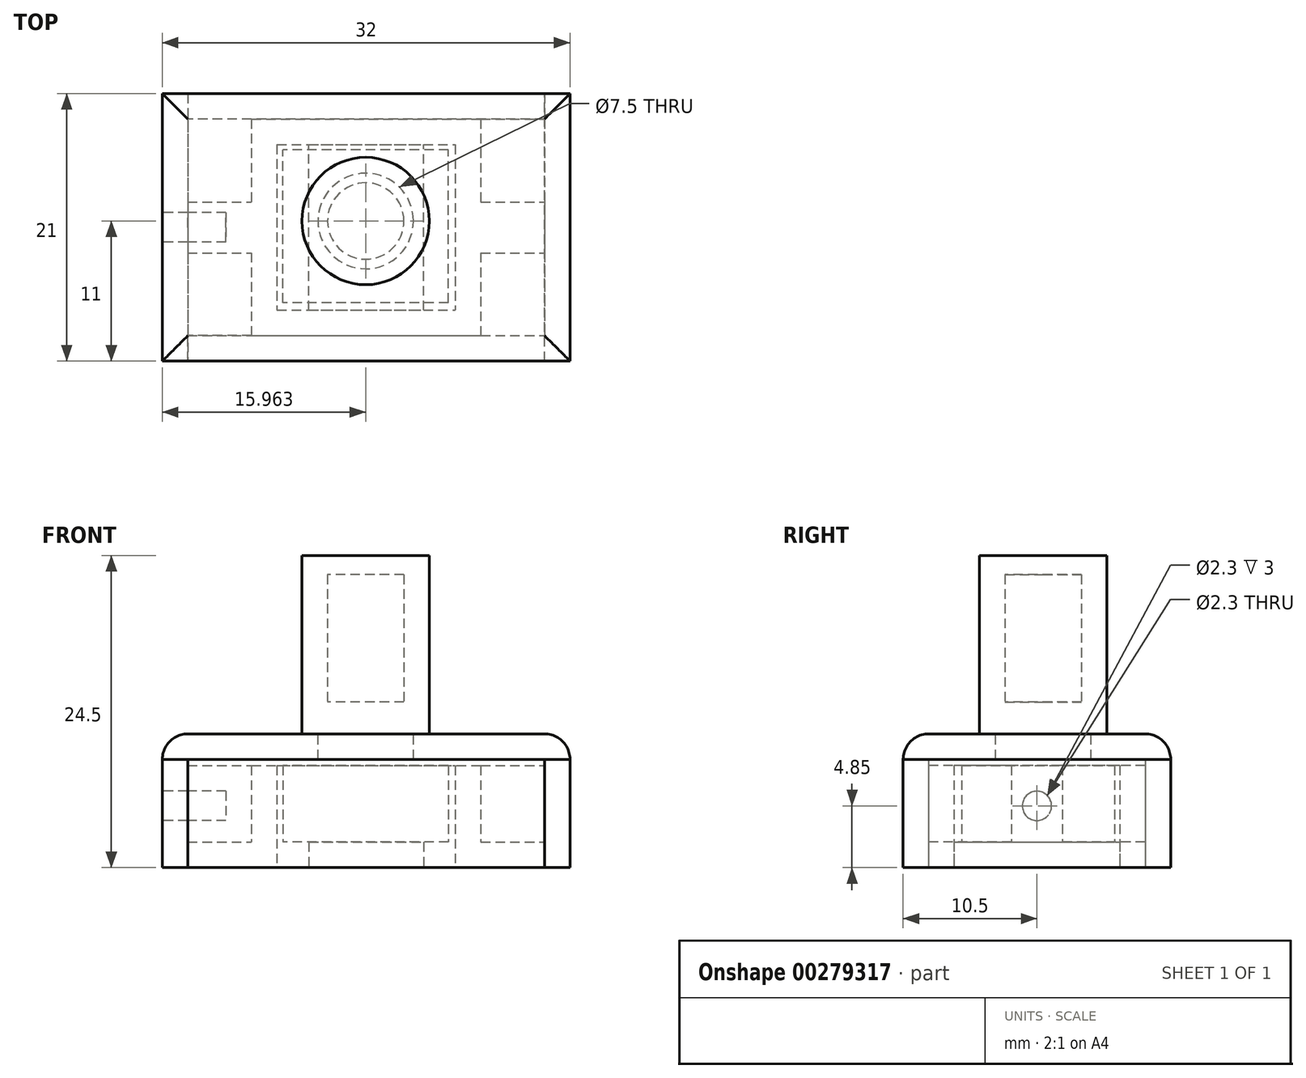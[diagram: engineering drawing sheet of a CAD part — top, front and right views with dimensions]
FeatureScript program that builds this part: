
annotation { "Feature Type Name" : "Feature", "Feature Type Description" : "" }
export const myFeature = defineFeature(function(context is Context, id is Id, definition is map)
    precondition{}
    {
        {
            var Q0;
            Q0=qCreatedBy(makeId("Top.planeOp"),FACE);
            var sketch = newSketch(context, id + "F0", { "sketchPlane" : qUnion([Q0])});
            skLineSegment(sketch, "E0.bottom", {"start": v(-2, 2) * mm, "end": v(16, 2) * mm});
            skLineSegment(sketch, "E0.top", {"start": v(-2, -15) * mm, "end": v(16, -15) * mm});
            skLineSegment(sketch, "E0.left", {"start": v(-2, 2) * mm, "end": v(-2, -15) * mm});
            skLineSegment(sketch, "E0.right", {"start": v(16, 2) * mm, "end": v(16, -15) * mm});
            skLineSegment(sketch, "E1.bottom", {"start": v(0, 0) * mm, "end": v(14, 0) * mm});
            skLineSegment(sketch, "E1.top", {"start": v(0, -13) * mm, "end": v(14, -13) * mm});
            skLineSegment(sketch, "E1.left", {"start": v(0, 0) * mm, "end": v(0, -13) * mm});
            skLineSegment(sketch, "E1.right", {"start": v(14, 0) * mm, "end": v(14, -13) * mm});
            skSolve(sketch);
        }
        {
            var Q0;
            Q0=qSketchRegion(id+"F0",true);
            extrude(context, id + "F1", {"entities" : qUnion([Q0]), "depth" : 8 * mm});
        }
        {
            var Q0;
            Q0=makeQuery(id+"F1.opExtrude","CAP_FACE",FACE,{"disambiguationData":[OSD([sQuery(id+"F0.wireOp",EDGE,"E0.bottom"),sQuery(id+"F0.wireOp",EDGE,"E0.top"),sQuery(id+"F0.wireOp",EDGE,"E0.left"),sQuery(id+"F0.wireOp",EDGE,"E0.right"),sQuery(id+"F0.wireOp",EDGE,"E1.bottom"),sQuery(id+"F0.wireOp",EDGE,"E1.top"),sQuery(id+"F0.wireOp",EDGE,"E1.left"),sQuery(id+"F0.wireOp",EDGE,"E1.right")])],"isStart":true});
            var sketch = newSketch(context, id + "F2", { "sketchPlane" : qUnion([Q0])});
            skLineSegment(sketch, "E2.bottom", {"start": v(2.5, 13) * mm, "end": v(11.5, 13) * mm});
            skLineSegment(sketch, "E2.top", {"start": v(2.5, 0) * mm, "end": v(11.5, 0) * mm});
            skLineSegment(sketch, "E2.left", {"start": v(2.5, 13) * mm, "end": v(2.5, 0) * mm});
            skLineSegment(sketch, "E2.right", {"start": v(11.5, 13) * mm, "end": v(11.5, 0) * mm});
            skSolve(sketch);
        }
        {
            var Q0;
            Q0=qSketchRegion(id+"F2",true);
            extrude(context, id + "F3", {"entities" : qUnion([Q0]), "operationType" : NewBodyOperationType.ADD, "oppositeDirection" : true, "depth" : 2 * mm});
        }
        {
            var Q0;
            Q0=makeQuery(id+"F3.opExtrude","CAP_FACE",FACE,{"disambiguationData":[OSD([sQuery(id+"F2.wireOp",EDGE,"E2.bottom"),sQuery(id+"F2.wireOp",EDGE,"E2.top"),sQuery(id+"F2.wireOp",EDGE,"E2.left"),sQuery(id+"F2.wireOp",EDGE,"E2.right")])],"isStart":false});
            var sketch = newSketch(context, id + "F4", { "sketchPlane" : qUnion([Q0])});
            skSolve(sketch);
        }
        {
            var Q0;
            Q0=makeQuery(id+"F4.imprint","IMPRINT",FACE,{"disambiguationData":[TD([[makeQuery(id+"F4.imprint","IMPRINT",EDGE,{"derivedFrom":makeQuery(id+"F3.opExtrude","CAP_EDGE",EDGE,{"disambiguationData":[OSD([sQuery(id+"F2.wireOp",EDGE,"E2.left")])],"isStart":false})}),-1.0]])]});
            var sketch = newSketch(context, id + "F5", { "sketchPlane" : qUnion([Q0])});
            skLineSegment(sketch, "E3.bottom", {"start": v(13.46, -12.41) * mm, "end": v(0.46, -12.41) * mm});
            skLineSegment(sketch, "E3.top", {"start": v(13.46, -0.41) * mm, "end": v(0.46, -0.41) * mm});
            skLineSegment(sketch, "E3.left", {"start": v(13.46, -12.41) * mm, "end": v(13.46, -0.41) * mm});
            skLineSegment(sketch, "E3.right", {"start": v(0.46, -12.41) * mm, "end": v(0.46, -0.41) * mm});
            skPoint(sketch, "E3.middle", {"position": v(6.96, -6.41) * mm});
            skSolve(sketch);
        }
        {
            var Q0;
            Q0=qSketchRegion(id+"F5",true);
            extrude(context, id + "F6", {"entities" : qUnion([Q0]), "depth" : 6 * mm});
        }
        {
            var Q0;
            Q0=makeQuery(id+"F6.opExtrude","CAP_FACE",FACE,{"disambiguationData":[OSD([sQuery(id+"F5.wireOp",EDGE,"E3.bottom"),sQuery(id+"F5.wireOp",EDGE,"E3.top"),sQuery(id+"F5.wireOp",EDGE,"E3.left"),sQuery(id+"F5.wireOp",EDGE,"E3.right")])],"isStart":false});
            var sketch = newSketch(context, id + "F7", { "sketchPlane" : qUnion([Q0])});
            skCircle(sketch, "E4", {"center": v(6.96, -6) * mm, "radius": 3.5 * mm});
            skSolve(sketch);
        }
        {
            var Q0;
            Q0=qSketchRegion(id+"F7",true);
            extrude(context, id + "F8", {"entities" : qUnion([Q0]), "depth" : 5 * mm});
        }
        {
            var Q0;
            Q0=makeQuery(id+"F8.opExtrude","CAP_FACE",FACE,{"disambiguationData":[OSD([sQuery(id+"F7.wireOp",EDGE,"E4")])],"isStart":false});
            var sketch = newSketch(context, id + "F9", { "sketchPlane" : qUnion([Q0])});
            skCircle(sketch, "E5", {"center": v(6.96, -6) * mm, "radius": 3 * mm});
            skSolve(sketch);
        }
        {
            var Q0;
            Q0=qSketchRegion(id+"F9",true);
            extrude(context, id + "F10", {"entities" : qUnion([Q0]), "depth" : 10 * mm});
        }
        {
            var Q0;
            Q0=qCreatedBy(makeId("Top.planeOp"),FACE);
            var sketch = newSketch(context, id + "F11", { "sketchPlane" : qUnion([Q0])});
            skLineSegment(sketch, "E6.bottom", {"start": v(-2, 2) * mm, "end": v(-7, 2) * mm});
            skLineSegment(sketch, "E6.top", {"start": v(-2, -15) * mm, "end": v(-7, -15) * mm});
            skLineSegment(sketch, "E6.left", {"start": v(-2, 2) * mm, "end": v(-2, -15) * mm});
            skLineSegment(sketch, "E6.right", {"start": v(-7, 2) * mm, "end": v(-7, -15) * mm});
            skLineSegment(sketch, "E7.bottom", {"start": v(16, 2) * mm, "end": v(21, 2) * mm});
            skLineSegment(sketch, "E7.top", {"start": v(16, -15) * mm, "end": v(21, -15) * mm});
            skLineSegment(sketch, "E7.left", {"start": v(16, 2) * mm, "end": v(16, -15) * mm});
            skLineSegment(sketch, "E7.right", {"start": v(21, 2) * mm, "end": v(21, -15) * mm});
            skSolve(sketch);
        }
        {
            var Q0;
            Q0=qSketchRegion(id+"F11",true);
            extrude(context, id + "F12", {"entities" : qUnion([Q0]), "operationType" : NewBodyOperationType.ADD, "depth" : 2 * mm});
        }
        {
            var Q0;
            Q0=makeQuery(id+"F12.opExtrude","CAP_FACE",FACE,{"disambiguationData":[OSD([sQuery(id+"F11.wireOp",EDGE,"E6.bottom"),sQuery(id+"F11.wireOp",EDGE,"E6.top"),sQuery(id+"F11.wireOp",EDGE,"E6.left"),sQuery(id+"F11.wireOp",EDGE,"E6.right"),sQuery(id+"F11.wireOp",EDGE,"gcyy9ogg-o8VV-Q8VI-mciE-UxV4sGVMyMyK"),sQuery(id+"F11.wireOp",EDGE,"7D3NRwDX-bBHB-H0ax-FCWy-7Xh7mBDSAGuq")])],"isStart":false});
            var sketch = newSketch(context, id + "F13", { "sketchPlane" : qUnion([Q0])});
            skLineSegment(sketch, "E8.bottom", {"start": v(-7, -4.5) * mm, "end": v(-2, -4.5) * mm});
            skLineSegment(sketch, "E8.top", {"start": v(-7, -8.5) * mm, "end": v(-2, -8.5) * mm});
            skLineSegment(sketch, "E8.left", {"start": v(-7, -4.5) * mm, "end": v(-7, -8.5) * mm});
            skLineSegment(sketch, "E8.right", {"start": v(-2, -4.5) * mm, "end": v(-2, -8.5) * mm});
            skLineSegment(sketch, "E9.bottom", {"start": v(16, -4.5) * mm, "end": v(21, -4.5) * mm});
            skLineSegment(sketch, "E9.top", {"start": v(16, -8.5) * mm, "end": v(21, -8.5) * mm});
            skLineSegment(sketch, "E9.left", {"start": v(16, -4.5) * mm, "end": v(16, -8.5) * mm});
            skLineSegment(sketch, "E9.right", {"start": v(21, -4.5) * mm, "end": v(21, -8.5) * mm});
            skSolve(sketch);
        }
        {
            var Q0;
            Q0=qSketchRegion(id+"F13",true);
            extrude(context, id + "F14", {"entities" : qUnion([Q0]), "operationType" : NewBodyOperationType.ADD, "depth" : 6 * mm});
        }
        {
            var Q0;
            Q0=makeQuery(id+"F12.boolean.opBoolean","MERGE",FACE,{"derivedFrom":[makeQuery(id+"F1.opExtrude","SWEPT_FACE",FACE,{"disambiguationData":[OSD([sQuery(id+"F0.wireOp",EDGE,"E0.top")])]}),makeQuery(id+"F12.opExtrude","SWEPT_FACE",FACE,{"disambiguationData":[OSD([sQuery(id+"F11.wireOp",EDGE,"E6.top")])]}),makeQuery(id+"F12.opExtrude","SWEPT_FACE",FACE,{"disambiguationData":[OSD([sQuery(id+"F11.wireOp",EDGE,"E7.top")])]})]});
            var sketch = newSketch(context, id + "F15", { "sketchPlane" : qUnion([Q0])});
            skLineSegment(sketch, "E10.bottom", {"start": v(-7, 0) * mm, "end": v(21, 0) * mm});
            skLineSegment(sketch, "E10.top", {"start": v(-7, 8.5) * mm, "end": v(21, 8.5) * mm});
            skLineSegment(sketch, "E10.left", {"start": v(-7, 0) * mm, "end": v(-7, 8.5) * mm});
            skLineSegment(sketch, "E10.right", {"start": v(21, 0) * mm, "end": v(21, 8.5) * mm});
            skSolve(sketch);
        }
        {
            var Q0;
            Q0=qSketchRegion(id+"F15",true);
            extrude(context, id + "F16", {"entities" : qUnion([Q0]), "depth" : 2 * mm});
        }
        {
            var Q0;
            Q0=makeQuery(id+"F14.opExtrude","SWEPT_FACE",FACE,{"disambiguationData":[OSD([sQuery(id+"F13.wireOp",EDGE,"E9.right")])]});
            var sketch = newSketch(context, id + "F17", { "sketchPlane" : qUnion([Q0])});
            skLineSegment(sketch, "E11.bottom", {"start": v(-17, 0) * mm, "end": v(4, 0) * mm});
            skLineSegment(sketch, "E11.top", {"start": v(-17, 8.5) * mm, "end": v(4, 8.5) * mm});
            skLineSegment(sketch, "E11.left", {"start": v(-17, 0) * mm, "end": v(-17, 8.5) * mm});
            skLineSegment(sketch, "E11.right", {"start": v(4, 0) * mm, "end": v(4, 8.5) * mm});
            skSolve(sketch);
        }
        {
            var Q0;
            Q0=qSketchRegion(id+"F17",true);
            extrude(context, id + "F18", {"entities" : qUnion([Q0]), "depth" : 2 * mm});
        }
        {
            var Q0;
            Q0=makeQuery(id+"F12.boolean.opBoolean","MERGE",FACE,{"derivedFrom":[makeQuery(id+"F1.opExtrude","SWEPT_FACE",FACE,{"disambiguationData":[OSD([sQuery(id+"F0.wireOp",EDGE,"E0.bottom")])]}),makeQuery(id+"F12.opExtrude","SWEPT_FACE",FACE,{"disambiguationData":[OSD([sQuery(id+"F11.wireOp",EDGE,"E6.bottom")])]}),makeQuery(id+"F12.opExtrude","SWEPT_FACE",FACE,{"disambiguationData":[OSD([sQuery(id+"F11.wireOp",EDGE,"E7.bottom")])]})]});
            var sketch = newSketch(context, id + "F19", { "sketchPlane" : qUnion([Q0])});
            skLineSegment(sketch, "E12.bottom", {"start": v(-21, 0) * mm, "end": v(7, 0) * mm});
            skLineSegment(sketch, "E12.top", {"start": v(-21, 8.5) * mm, "end": v(7, 8.5) * mm});
            skLineSegment(sketch, "E12.left", {"start": v(-21, 0) * mm, "end": v(-21, 8.5) * mm});
            skLineSegment(sketch, "E12.right", {"start": v(7, 0) * mm, "end": v(7, 8.5) * mm});
            skSolve(sketch);
        }
        {
            var Q0;
            Q0=qSketchRegion(id+"F19",true);
            extrude(context, id + "F20", {"entities" : qUnion([Q0]), "depth" : 2 * mm});
        }
        {
            var Q0;
            Q0=makeQuery(id+"F14.boolean.opBoolean","MERGE",FACE,{"derivedFrom":[makeQuery(id+"F12.opExtrude","SWEPT_FACE",FACE,{"disambiguationData":[OSD([sQuery(id+"F11.wireOp",EDGE,"E6.right")])]}),makeQuery(id+"F14.opExtrude","SWEPT_FACE",FACE,{"disambiguationData":[OSD([sQuery(id+"F13.wireOp",EDGE,"E8.left")])]})]});
            var sketch = newSketch(context, id + "F21", { "sketchPlane" : qUnion([Q0])});
            skLineSegment(sketch, "E13.bottom", {"start": v(-4, 0) * mm, "end": v(17, 0) * mm});
            skLineSegment(sketch, "E13.top", {"start": v(-4, 8.5) * mm, "end": v(17, 8.5) * mm});
            skLineSegment(sketch, "E13.left", {"start": v(-4, 0) * mm, "end": v(-4, 8.5) * mm});
            skLineSegment(sketch, "E13.right", {"start": v(17, 0) * mm, "end": v(17, 8.5) * mm});
            skSolve(sketch);
        }
        {
            var Q0;
            Q0=qSketchRegion(id+"F21",true);
            extrude(context, id + "F22", {"entities" : qUnion([Q0]), "depth" : 2 * mm});
        }
        {
            var Q0;
            Q0=makeQuery(id+"F22.opExtrude","CAP_FACE",FACE,{"disambiguationData":[OSD([sQuery(id+"F21.wireOp",EDGE,"E13.bottom"),sQuery(id+"F21.wireOp",EDGE,"E13.top"),sQuery(id+"F21.wireOp",EDGE,"E13.left"),sQuery(id+"F21.wireOp",EDGE,"E13.right")])],"isStart":false});
            var sketch = newSketch(context, id + "F23", { "sketchPlane" : qUnion([Q0])});
            skCircle(sketch, "E14", {"center": v(6.5, 4.85) * mm, "radius": 1.15 * mm});
            skSolve(sketch);
        }
        {
            var Q0;
            Q0=qSketchRegion(id+"F23",true);
            extrude(context, id + "F24", {"entities" : qUnion([Q0]), "operationType" : NewBodyOperationType.REMOVE, "oppositeDirection" : true, "depth" : 5 * mm});
        }
        {
            var Q0;
            Q0=makeQuery(id+"F20.opExtrude","SWEPT_FACE",FACE,{"disambiguationData":[OSD([sQuery(id+"F19.wireOp",EDGE,"E12.top")])]});
            var sketch = newSketch(context, id + "F25", { "sketchPlane" : qUnion([Q0])});
            skLineSegment(sketch, "E15.bottom", {"start": v(-9, 4) * mm, "end": v(23, 4) * mm});
            skLineSegment(sketch, "E15.top", {"start": v(-9, -17) * mm, "end": v(23, -17) * mm});
            skLineSegment(sketch, "E15.left", {"start": v(-9, 4) * mm, "end": v(-9, -17) * mm});
            skLineSegment(sketch, "E15.right", {"start": v(23, 4) * mm, "end": v(23, -17) * mm});
            skSolve(sketch);
        }
        {
            var Q0;
            Q0=qSketchRegion(id+"F25",true);
            extrude(context, id + "F26", {"entities" : qUnion([Q0]), "depth" : 2 * mm});
        }
        {
            var Q0;
            Q0=makeQuery(id+"F8.opExtrude","CAP_FACE",FACE,{"disambiguationData":[OSD([sQuery(id+"F7.wireOp",EDGE,"E4")])],"isStart":false});
            var sketch = newSketch(context, id + "F27", { "sketchPlane" : qUnion([Q0])});
            skCircle(sketch, "E16", {"center": v(6.96, -6) * mm, "radius": 3.75 * mm});
            skSolve(sketch);
        }
        {
            var Q0;
            Q0=qSketchRegion(id+"F27",true);
            extrude(context, id + "F28", {"entities" : qUnion([Q0]), "operationType" : NewBodyOperationType.REMOVE, "oppositeDirection" : true, "depth" : 5 * mm});
        }
        {
            var Q0;
            Q0=makeQuery(id+"F26.opExtrude","CAP_FACE",FACE,{"disambiguationData":[OSD([sQuery(id+"F25.wireOp",EDGE,"E15.bottom"),sQuery(id+"F25.wireOp",EDGE,"E15.top"),sQuery(id+"F25.wireOp",EDGE,"E15.left"),sQuery(id+"F25.wireOp",EDGE,"E15.right")])],"isStart":false});
            var sketch = newSketch(context, id + "F29", { "sketchPlane" : qUnion([Q0])});
            skCircle(sketch, "E17", {"center": v(6.96, -6) * mm, "radius": 5 * mm});
            skSolve(sketch);
        }
        {
            var Q0;
            Q0=qSketchRegion(id+"F29",true);
            extrude(context, id + "F30", {"entities" : qUnion([Q0]), "depth" : 14 * mm});
        }
        {
            var Q0;
            Q0=makeQuery(id+"F26.opExtrude","CAP_EDGE",EDGE,{"disambiguationData":[OSD([sQuery(id+"F25.wireOp",EDGE,"E15.left")])],"isStart":false});
            var Q1;
            Q1=makeQuery(id+"F26.opExtrude","CAP_EDGE",EDGE,{"disambiguationData":[OSD([sQuery(id+"F25.wireOp",EDGE,"E15.bottom")])],"isStart":false});
            var Q2;
            Q2=makeQuery(id+"F26.opExtrude","CAP_EDGE",EDGE,{"disambiguationData":[OSD([sQuery(id+"F25.wireOp",EDGE,"E15.top")])],"isStart":false});
            var Q3;
            Q3=makeQuery(id+"F26.opExtrude","CAP_EDGE",EDGE,{"disambiguationData":[OSD([sQuery(id+"F25.wireOp",EDGE,"E15.right")])],"isStart":false});
            fillet(context, id + "F31", {"entities" : qUnion([Q0, Q1, Q2, Q3]), "radius" : 2 * mm, "tangentPropagation" : true, "allowEdgeOverflow" : false});
        }
    });
